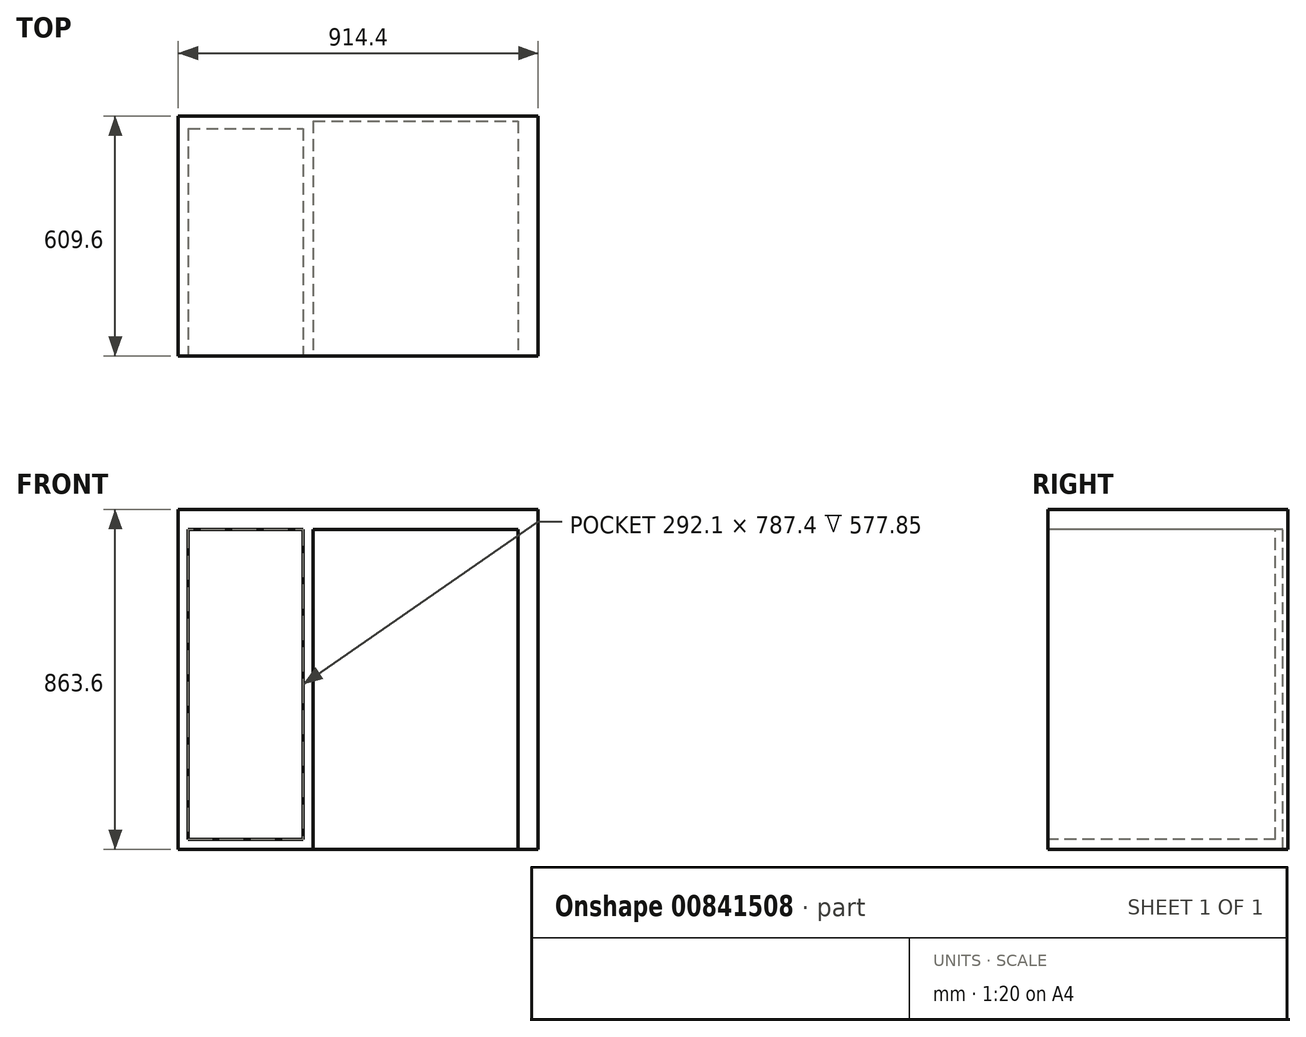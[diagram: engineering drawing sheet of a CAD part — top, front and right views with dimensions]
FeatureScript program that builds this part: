
annotation { "Feature Type Name" : "Feature", "Feature Type Description" : "" }
export const myFeature = defineFeature(function(context is Context, id is Id, definition is map)
    precondition{}
    {
        {
            var Q0;
            Q0=qCreatedBy(makeId("Front.planeOp"),FACE);
            var sketch = newSketch(context, id + "F0", { "sketchPlane" : qUnion([Q0])});
            skLineSegment(sketch, "E0.bottom", {"start": v(0, 0) * mm, "end": v(914.4, 0) * mm});
            skLineSegment(sketch, "E0.top", {"start": v(0, 863.6) * mm, "end": v(914.4, 863.6) * mm});
            skLineSegment(sketch, "E0.left", {"start": v(0, 0) * mm, "end": v(0, 863.6) * mm});
            skLineSegment(sketch, "E0.right", {"start": v(914.4, 0) * mm, "end": v(914.4, 863.6) * mm});
            skSolve(sketch);
        }
        {
            var Q0;
            Q0=qSketchRegion(id+"F0",true);
            extrude(context, id + "F1", {"entities" : qUnion([Q0]), "depth" : 609.6 * mm, "offsetDistance" : 25.4 * mm});
        }
        {
            var Q0;
            Q0=makeQuery(id+"F1.opExtrude","CAP_FACE",FACE,{"disambiguationData":[OSD([sQuery(id+"F0.wireOp",EDGE,"E0.bottom"),sQuery(id+"F0.wireOp",EDGE,"E0.top"),sQuery(id+"F0.wireOp",EDGE,"E0.left"),sQuery(id+"F0.wireOp",EDGE,"E0.right")])],"isStart":false});
            var sketch = newSketch(context, id + "F2", { "sketchPlane" : qUnion([Q0])});
            skLineSegment(sketch, "E1.bottom", {"start": v(863.6, 0) * mm, "end": v(342.9, 0) * mm});
            skLineSegment(sketch, "E1.top", {"start": v(863.6, 812.8) * mm, "end": v(342.9, 812.8) * mm});
            skLineSegment(sketch, "E1.left", {"start": v(863.6, 0) * mm, "end": v(863.6, 812.8) * mm});
            skLineSegment(sketch, "E1.right", {"start": v(342.9, 0) * mm, "end": v(342.9, 812.8) * mm});
            skSolve(sketch);
        }
        {
            var Q0;
            Q0=qSketchRegion(id+"F2",true);
            extrude(context, id + "F3", {"entities" : qUnion([Q0]), "operationType" : NewBodyOperationType.REMOVE, "oppositeDirection" : true, "depth" : 596.9 * mm, "offsetDistance" : 25.4 * mm});
        }
        {
            var Q0;
            Q0=makeQuery(id+"F1.opExtrude","CAP_FACE",FACE,{"disambiguationData":[OSD([sQuery(id+"F0.wireOp",EDGE,"E0.bottom"),sQuery(id+"F0.wireOp",EDGE,"E0.top"),sQuery(id+"F0.wireOp",EDGE,"E0.left"),sQuery(id+"F0.wireOp",EDGE,"E0.right")])],"isStart":false});
            var sketch = newSketch(context, id + "F4", { "sketchPlane" : qUnion([Q0])});
            skLineSegment(sketch, "E2.bottom", {"start": v(25.4, 25.4) * mm, "end": v(317.5, 25.4) * mm});
            skLineSegment(sketch, "E2.top", {"start": v(25.4, 812.8) * mm, "end": v(317.5, 812.8) * mm});
            skLineSegment(sketch, "E2.left", {"start": v(25.4, 25.4) * mm, "end": v(25.4, 812.8) * mm});
            skLineSegment(sketch, "E2.right", {"start": v(317.5, 25.4) * mm, "end": v(317.5, 812.8) * mm});
            skSolve(sketch);
        }
        {
            var Q0;
            Q0=qSketchRegion(id+"F4",true);
            extrude(context, id + "F5", {"entities" : qUnion([Q0]), "operationType" : NewBodyOperationType.REMOVE, "oppositeDirection" : true, "depth" : 577.85 * mm, "offsetDistance" : 25.4 * mm});
        }
    });
